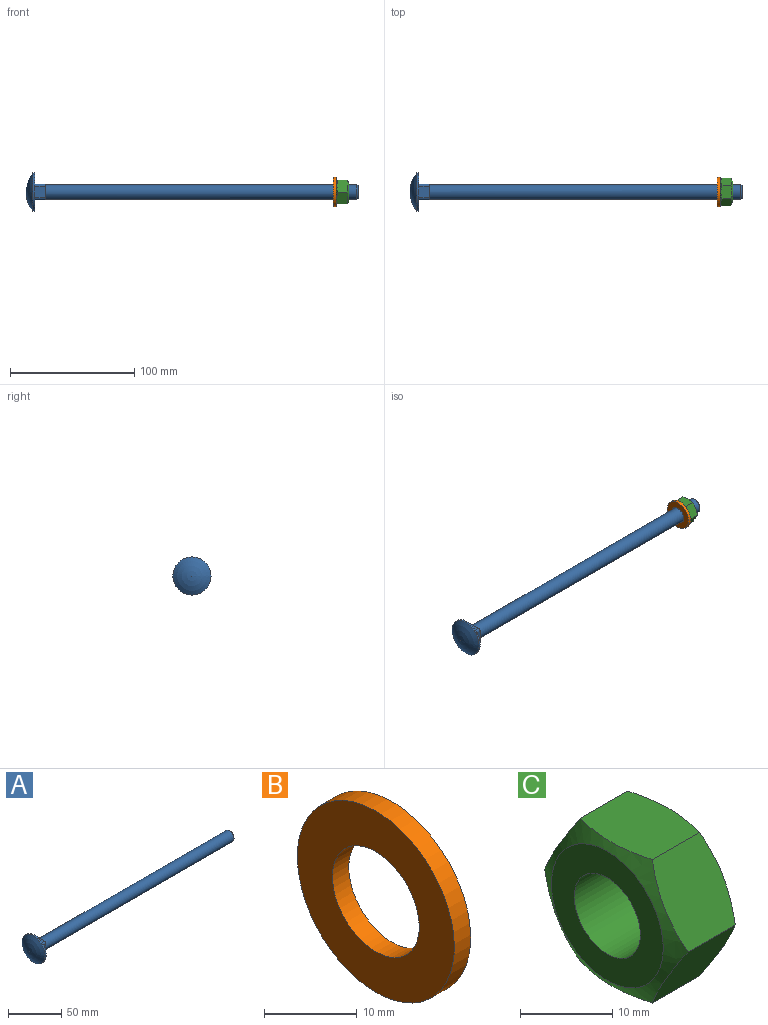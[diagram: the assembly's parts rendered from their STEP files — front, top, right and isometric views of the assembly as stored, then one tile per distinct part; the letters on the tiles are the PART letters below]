
ASSEMBLY  parts=3 mates=2
PART A: 15 faces, bbox 267x30.7x30.7 mm
  f0: plane 9.1x8.75mm, normal (0,1,0), area 79.6mm2, adj f4,f5,f10,f11
  f1: plane 9.1x8.75mm, normal (0,0,1), area 79.6mm2, adj f4,f5,f8,f11
  f2: plane 9.1x8.75mm, normal (0,-1,0), area 79.6mm2, adj f4,f5,f8,f9
  f3: plane 9.1x8.75mm, normal (0,0,-1), area 79.6mm2, adj f4,f5,f9,f10
  f4: plane 12.7x12.7mm, normal (1,0,0), area 45.4mm2, adj f0,f1,f2,f3,f8,f9,f10,f11
  f5: plane 30.65x30.65mm, normal (1,0,0), area 579.3mm2, adj f0,f1,f2,f3,f6,f8,f9,f10
  f6: cylinder r=15.32mm len=30.65mm, axis (-1,0,0), area 139.6mm2, adj f5,f7
  f7: sphere r=24.1mm, area 832.9mm2, adj f6
  f8: cylinder r=1.8mm len=8.75mm, axis (-1,0,0), area 24.7mm2, adj f1,f2,f4,f5
  f9: cylinder r=1.8mm len=8.75mm, axis (-1,0,0), area 24.7mm2, adj f2,f3,f4,f5
  f10: cylinder r=1.8mm len=8.75mm, axis (-1,0,0), area 24.7mm2, adj f0,f3,f4,f5
  f11: cylinder r=1.8mm len=8.75mm, axis (-1,0,0), area 24.7mm2, adj f0,f1,f4,f5
  f12: cylinder r=6mm len=250.25mm, axis (1,0,0), area 9434.2mm2, adj f4,f14
  f13: plane 10x10mm, normal (1,0,0), area 78.5mm2, adj f14
  f14: cone r=5mm half-angle=45deg, axis (-1,0,0), area 48.9mm2, adj f12,f13
PART B: 4 faces, bbox 2.5x24x24 mm
  f0: cylinder r=6.64mm len=13.27mm, axis (1,0,0), area 104.2mm2, adj f2,f3
  f1: cylinder r=12mm len=24mm, axis (1,0,0), area 188.5mm2, adj f2,f3
  f2: plane 24x24mm, normal (-1,0,0), area 314.1mm2, adj f0,f1
  f3: plane 24x24mm, normal (1,0,0), area 314.1mm2, adj f0,f1
PART C: 11 faces, bbox 10x21.9x21.9 mm
  f0: plane 17.1x17.1mm, normal (1,0,0), area 149.4mm2, adj f1,f4
  f1: cone r=11.4mm half-angle=60deg, axis (-1,0,0), area 95.8mm2, adj f0,f5,f6,f7,f8,f9,f10
  f2: cone r=8.55mm half-angle=60deg, axis (1,0,0), area 95.8mm2, adj f3,f5,f6,f7,f8,f9,f10
  f3: plane 17.1x17.1mm, normal (-1,0,0), area 149.4mm2, adj f2,f4
  f4: cylinder r=5.05mm len=10.11mm, axis (1,0,0), area 317.5mm2, adj f0,f3
  f5: plane 10.98x8.91mm, normal (0,0,1), area 91.3mm2, adj f1,f2,f6,f10
  f6: plane 9.5x8.91mm, normal (0,0.87,0.5), area 91.3mm2, adj f1,f2,f5,f7
  f7: plane 9.5x8.91mm, normal (0,0.87,-0.5), area 91.3mm2, adj f1,f2,f6,f8
  f8: plane 10.98x8.91mm, normal (0,0,-1), area 91.3mm2, adj f1,f2,f7,f9
  f9: plane 9.5x8.91mm, normal (0,-0.87,-0.5), area 91.3mm2, adj f1,f2,f8,f10
  f10: plane 9.5x8.91mm, normal (0,-0.87,0.5), area 91.3mm2, adj f1,f2,f5,f9
PLACE A at identity fixed
PLACE B t=(240,0,0)mm
PLACE C t=(242.5,0,0)mm
MATE fastened A.f12 <-> B.f0  axis (1,0,0) through (0,0,0)mm
MATE fastened B.f0 <-> C.f1  axis (1,0,0) through (242.5,0,0)mm
